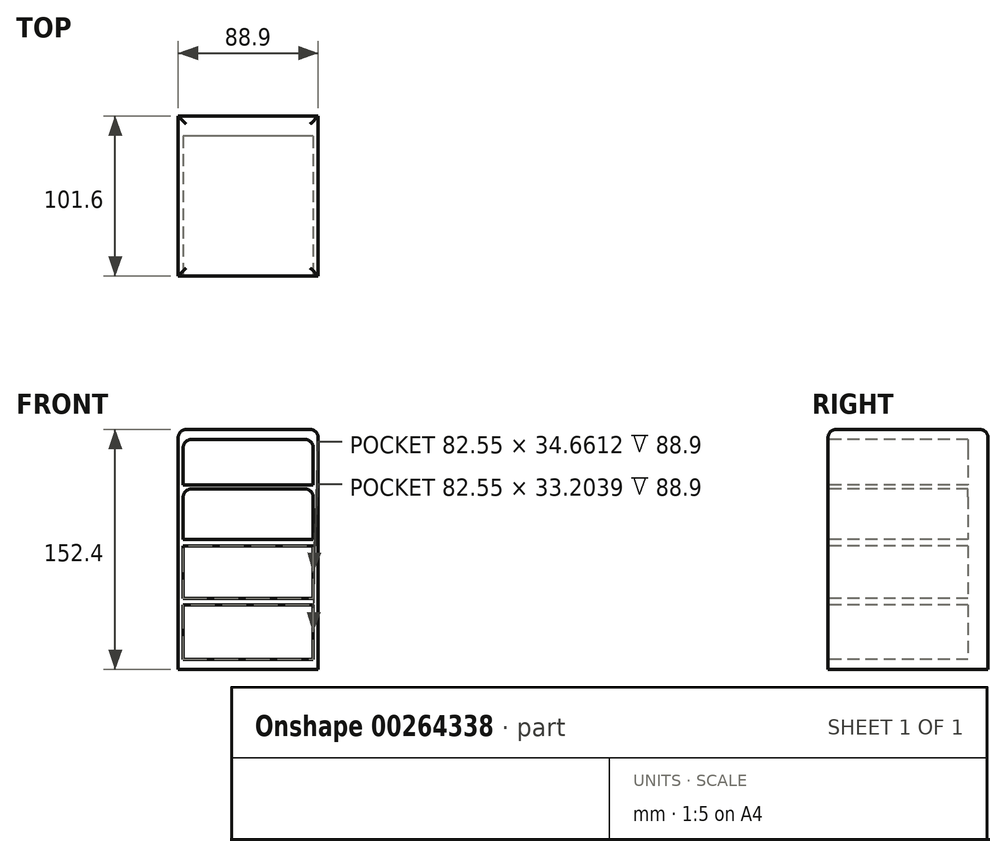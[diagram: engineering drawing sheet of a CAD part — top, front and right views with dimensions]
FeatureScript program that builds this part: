
annotation { "Feature Type Name" : "Feature", "Feature Type Description" : "" }
export const myFeature = defineFeature(function(context is Context, id is Id, definition is map)
    precondition{}
    {
        {
            var Q0;
            Q0=qCreatedBy(makeId("Front.planeOp"),FACE);
            var sketch = newSketch(context, id + "F0", { "sketchPlane" : qUnion([Q0])});
            skLineSegment(sketch, "E0.bottom", {"start": v(-44.45, 76.2) * mm, "end": v(44.45, 76.2) * mm});
            skLineSegment(sketch, "E0.top", {"start": v(-44.45, -76.2) * mm, "end": v(44.45, -76.2) * mm});
            skLineSegment(sketch, "E0.left", {"start": v(-44.45, 76.2) * mm, "end": v(-44.45, -76.2) * mm});
            skLineSegment(sketch, "E0.right", {"start": v(44.45, 76.2) * mm, "end": v(44.45, -76.2) * mm});
            skPoint(sketch, "E0.middle", {"position": v(0, 0) * mm});
            skSolve(sketch);
        }
        {
            var Q0;
            Q0 = qSketchRegion(id + "F0", true);
            extrude(context, id + "F1", {"entities" : qUnion([Q0]), "endBound" : BoundingType.SYMMETRIC, "depth" : 101.6 * mm});
        }
        {
            var Q0;
            Q0=makeQuery(id+"F1.opExtrude","CAP_FACE",FACE,{"disambiguationData":[OSD([sQuery(id+"F0.wireOp",EDGE,"E0.bottom"),sQuery(id+"F0.wireOp",EDGE,"E0.top"),sQuery(id+"F0.wireOp",EDGE,"E0.left"),sQuery(id+"F0.wireOp",EDGE,"E0.right")])],"isStart":false});
            var sketch = newSketch(context, id + "F2", { "sketchPlane" : qUnion([Q0])});
            skLineSegment(sketch, "E1.bottom", {"start": v(-41.27, 69.85) * mm, "end": v(41.28, 69.85) * mm});
            skLineSegment(sketch, "E1.top", {"start": v(-41.28, -69.85) * mm, "end": v(41.27, -69.85) * mm});
            skLineSegment(sketch, "E1.left", {"start": v(-41.27, 69.85) * mm, "end": v(-41.28, -69.85) * mm});
            skLineSegment(sketch, "E1.right", {"start": v(41.28, 69.85) * mm, "end": v(41.27, -69.85) * mm});
            skPoint(sketch, "E1.middle", {"position": v(0, 0) * mm});
            skLineSegment(sketch, "E2", {"start": v(-41.28, 40.99) * mm, "end": v(41.27, 40.99) * mm});
            skLineSegment(sketch, "E3", {"start": v(41.28, 40.99) * mm, "end": v(41.28, 38.45) * mm});
            skLineSegment(sketch, "E4", {"start": v(41.28, 38.45) * mm, "end": v(-41.27, 38.45) * mm});
            skLineSegment(sketch, "E5", {"start": v(-41.28, 6.22) * mm, "end": v(41.28, 6.22) * mm});
            skLineSegment(sketch, "E6", {"start": v(41.28, 6.22) * mm, "end": v(41.28, 2.12) * mm});
            skLineSegment(sketch, "E7", {"start": v(41.28, 2.12) * mm, "end": v(-41.28, 2.12) * mm});
            skLineSegment(sketch, "E8", {"start": v(-41.28, -31.09) * mm, "end": v(41.27, -31.09) * mm});
            skLineSegment(sketch, "E9", {"start": v(41.27, -31.09) * mm, "end": v(41.27, -35.19) * mm});
            skLineSegment(sketch, "E10", {"start": v(41.27, -35.19) * mm, "end": v(-41.28, -35.19) * mm});
            skSolve(sketch);
        }
        {
            var Q0;
            {var subQ0=sQuery(id+"F2.wireOp",EDGE,"E1.bottom");Q0=makeQuery(id+"F2.imprint","IMPRINT",FACE,{"disambiguationData":[TD([[makeQuery(id+"F2.imprint","IMPRINT",EDGE,{"derivedFrom":subQ0}),-1.0]])]});}
            var Q1;
            {var subQ0=sQuery(id+"F2.wireOp",EDGE,"E4");Q1=makeQuery(id+"F2.imprint","IMPRINT",FACE,{"disambiguationData":[TD([[makeQuery(id+"F2.imprint","IMPRINT",EDGE,{"derivedFrom":subQ0}),1.0]])]});}
            var Q2;
            {var subQ0=sQuery(id+"F2.wireOp",EDGE,"E7");Q2=makeQuery(id+"F2.imprint","IMPRINT",FACE,{"disambiguationData":[TD([[makeQuery(id+"F2.imprint","IMPRINT",EDGE,{"derivedFrom":subQ0}),1.0]])]});}
            var Q3;
            {var subQ0=sQuery(id+"F2.wireOp",EDGE,"E1.top");Q3=makeQuery(id+"F2.imprint","IMPRINT",FACE,{"disambiguationData":[TD([[makeQuery(id+"F2.imprint","IMPRINT",EDGE,{"derivedFrom":subQ0}),1.0]])]});}
            extrude(context, id + "F3", {"entities" : qUnion([Q0, Q1, Q2, Q3]), "operationType" : NewBodyOperationType.REMOVE, "oppositeDirection" : true, "depth" : 88.9 * mm});
        }
        {
            var Q0;
            Q0=makeQuery(id+"F1.opExtrude","SWEPT_EDGE",EDGE,{"disambiguationData":[OSD([sQuery(id+"F0.wireOp",EDGE,"E0.bottom"),sQuery(id+"F0.wireOp",EDGE,"E0.left")])]});
            var Q1;
            Q1=makeQuery(id+"F1.opExtrude","SWEPT_EDGE",EDGE,{"disambiguationData":[OSD([sQuery(id+"F0.wireOp",EDGE,"E0.bottom"),sQuery(id+"F0.wireOp",EDGE,"E0.right")])]});
            var Q2;
            Q2=makeQuery(id+"F1.opExtrude","CAP_EDGE",EDGE,{"disambiguationData":[OSD([sQuery(id+"F0.wireOp",EDGE,"E0.bottom")])],"isStart":true});
            var Q3;
            Q3=makeQuery(id+"F1.opExtrude","CAP_EDGE",EDGE,{"disambiguationData":[OSD([sQuery(id+"F0.wireOp",EDGE,"E0.bottom")])],"isStart":false});
            var Q4;
            Q4=makeQuery(id+"F3.boolean.opBoolean","COPY",EDGE,{"derivedFrom":makeQuery(id+"F3.opExtrude","SWEPT_EDGE",EDGE,{"disambiguationData":[OSD([sQuery(id+"F2.wireOp",EDGE,"E1.left"),sQuery(id+"F2.wireOp",EDGE,"E4")])]})});
            var Q5;
            Q5=makeQuery(id+"F3.boolean.opBoolean","COPY",EDGE,{"derivedFrom":makeQuery(id+"F3.opExtrude","SWEPT_EDGE",EDGE,{"disambiguationData":[OSD([sQuery(id+"F2.wireOp",EDGE,"E1.right"),sQuery(id+"F2.wireOp",EDGE,"E3"),sQuery(id+"F2.wireOp",EDGE,"E4")])]})});
            var Q6;
            Q6=makeQuery(id+"F3.boolean.opBoolean","COPY",EDGE,{"derivedFrom":makeQuery(id+"F3.opExtrude","SWEPT_EDGE",EDGE,{"disambiguationData":[OSD([sQuery(id+"F2.wireOp",EDGE,"E1.bottom"),sQuery(id+"F2.wireOp",EDGE,"E1.right")])]})});
            var Q7;
            Q7=makeQuery(id+"F3.boolean.opBoolean","COPY",EDGE,{"derivedFrom":makeQuery(id+"F3.opExtrude","SWEPT_EDGE",EDGE,{"disambiguationData":[OSD([sQuery(id+"F2.wireOp",EDGE,"E1.bottom"),sQuery(id+"F2.wireOp",EDGE,"E1.left")])]})});
            fillet(context, id + "F4", {"entities" : qUnion([Q0, Q1, Q2, Q3, Q4, Q5, Q6, Q7]), "radius" : 5.08 * mm, "tangentPropagation" : true, "allowEdgeOverflow" : false});
        }
    });
